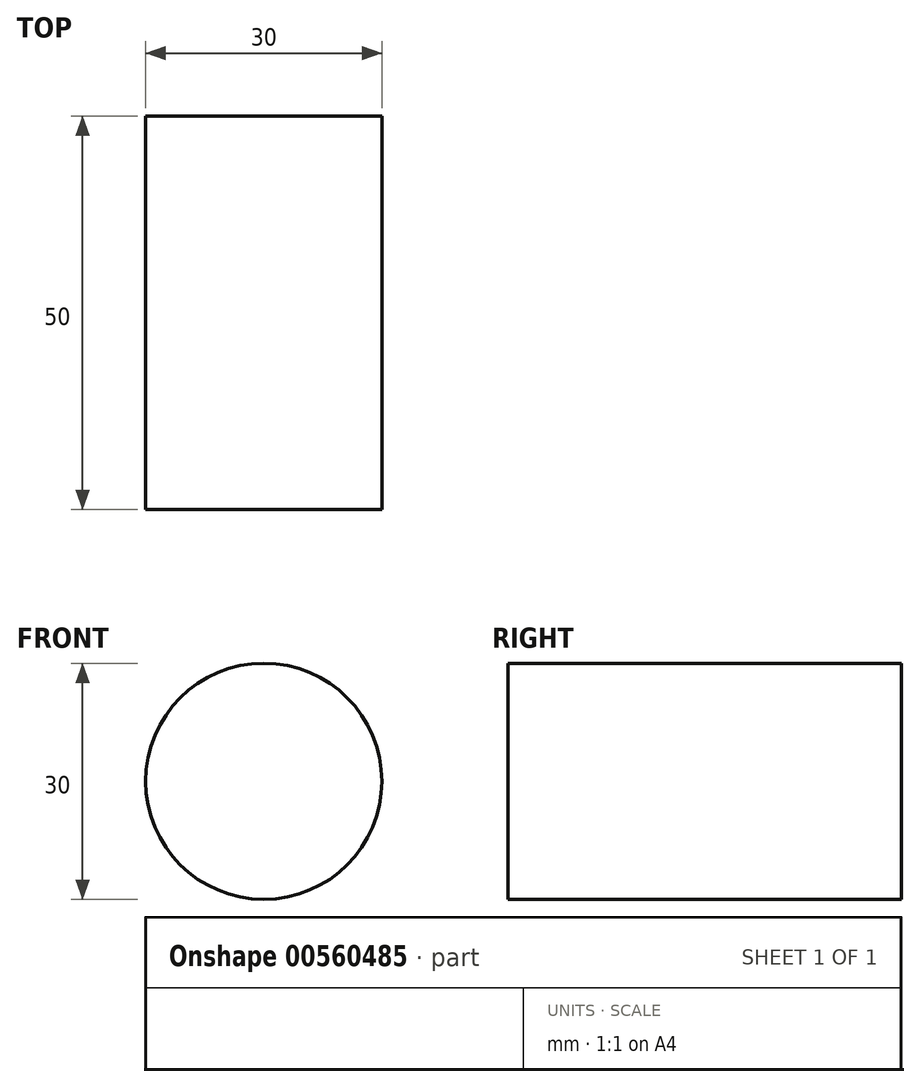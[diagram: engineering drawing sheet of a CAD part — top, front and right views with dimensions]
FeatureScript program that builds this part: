
annotation { "Feature Type Name" : "Feature", "Feature Type Description" : "" }
export const myFeature = defineFeature(function(context is Context, id is Id, definition is map)
    precondition{}
    {
        {
            var Q0;
            Q0=qCreatedBy(makeId("Front.planeOp"),FACE);
            var sketch = newSketch(context, id + "F0", { "sketchPlane" : qUnion([Q0])});
            skCircle(sketch, "E0", {"center": v(35.47, 27.97) * mm, "radius": 15 * mm});
            skSolve(sketch);
        }
        {
            var Q0;
            Q0=makeQuery(id+"F0.imprint","IMPRINT",FACE,{"disambiguationData":[TD([[makeQuery(id+"F0.imprint","IMPRINT",EDGE,{"derivedFrom":sQuery(id+"F0.wireOp",EDGE,"E0")}),1.0]])]});
            extrude(context, id + "F1", {"entities" : qUnion([Q0]), "depth" : 50 * mm, "offsetDistance" : 25 * mm});
        }
    });
